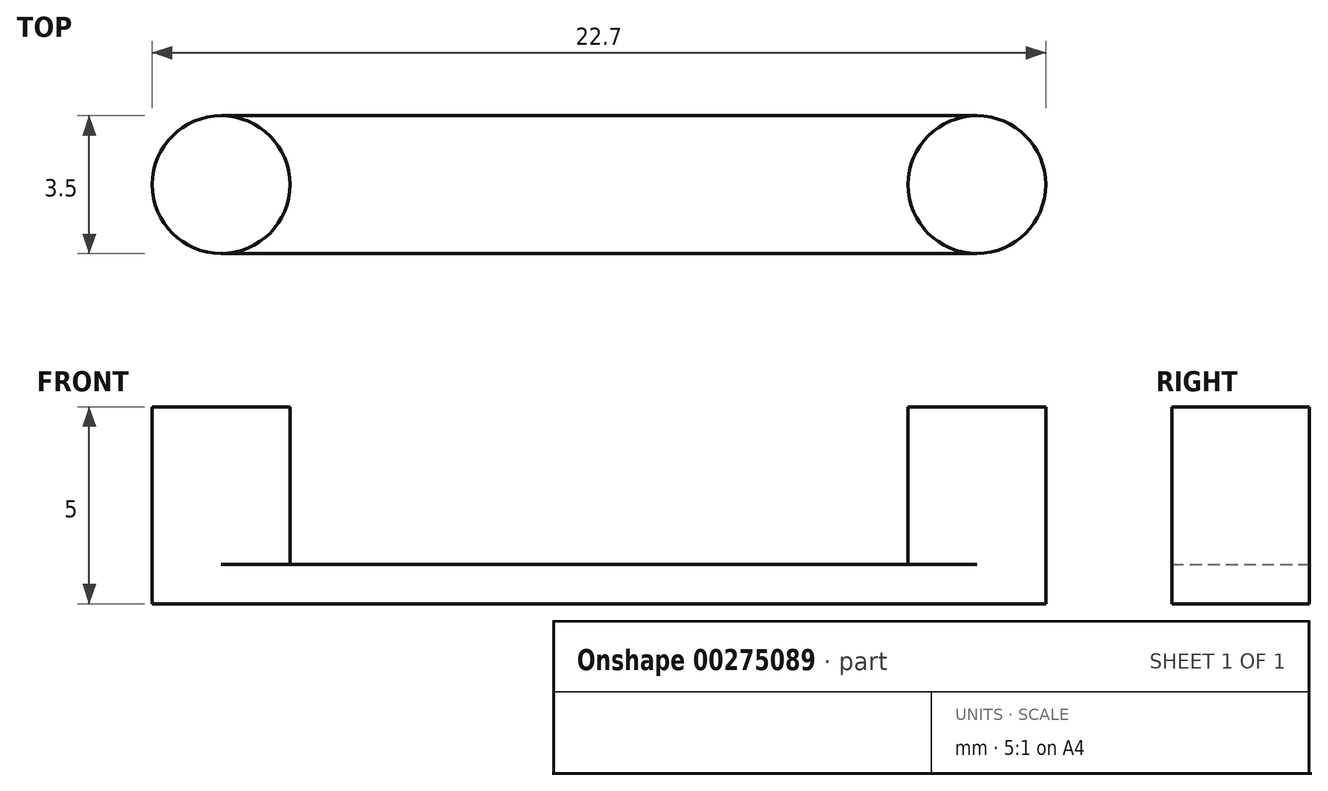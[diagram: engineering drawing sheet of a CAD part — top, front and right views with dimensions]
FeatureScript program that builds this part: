
annotation { "Feature Type Name" : "Feature", "Feature Type Description" : "" }
export const myFeature = defineFeature(function(context is Context, id is Id, definition is map)
    precondition{}
    {
        {
            var Q0;
            Q0=qCreatedBy(makeId("Top.planeOp"),FACE);
            var sketch = newSketch(context, id + "F0", { "sketchPlane" : qUnion([Q0])});
            skLineSegment(sketch, "E0.bottom", {"start": v(9.6, -9.6) * mm, "end": v(-9.6, -9.6) * mm, "construction": true});
            skLineSegment(sketch, "E0.top", {"start": v(9.6, 9.6) * mm, "end": v(-9.6, 9.6) * mm, "construction": true});
            skLineSegment(sketch, "E0.left", {"start": v(9.6, -9.6) * mm, "end": v(9.6, 9.6) * mm, "construction": true});
            skLineSegment(sketch, "E0.right", {"start": v(-9.6, -9.6) * mm, "end": v(-9.6, 9.6) * mm, "construction": true});
            skPoint(sketch, "E0.middle", {"position": v(0, 0) * mm});
            skPoint(sketch, "E1", {"position": v(-9.6, 0) * mm});
            skPoint(sketch, "E2", {"position": v(9.6, 0) * mm});
            skLineSegment(sketch, "E3", {"start": v(9.6, 0) * mm, "end": v(-9.6, 0) * mm});
            skCircle(sketch, "E4", {"center": v(-9.6, 0) * mm, "radius": 1.75 * mm});
            skCircle(sketch, "E5", {"center": v(9.6, 0) * mm, "radius": 1.75 * mm});
            skLineSegment(sketch, "E6.bottom", {"start": v(-9.6, -1.75) * mm, "end": v(9.6, -1.75) * mm});
            skLineSegment(sketch, "E6.top", {"start": v(-9.6, 1.75) * mm, "end": v(9.6, 1.75) * mm});
            skLineSegment(sketch, "E6.left", {"start": v(-9.6, -1.75) * mm, "end": v(-9.6, 1.75) * mm});
            skLineSegment(sketch, "E6.right", {"start": v(9.6, -1.75) * mm, "end": v(9.6, 1.75) * mm});
            skSolve(sketch);
        }
        {
            var Q0;
            {var subQ5=sQuery(id+"F0.wireOp",EDGE,"E6.top");Q0=makeQuery(id+"F0.imprint","IMPRINT",FACE,{"disambiguationData":[TD([[makeQuery(id+"F0.imprint","IMPRINT",EDGE,{"derivedFrom":subQ5}),-1.0]])]});}
            var Q1;
            {var subQ5=sQuery(id+"F0.wireOp",EDGE,"E6.bottom");Q1=makeQuery(id+"F0.imprint","IMPRINT",FACE,{"disambiguationData":[TD([[makeQuery(id+"F0.imprint","IMPRINT",EDGE,{"derivedFrom":subQ5}),1.0]])]});}
            extrude(context, id + "F1", {"entities" : qUnion([Q0, Q1]), "depth" : 1 * mm});
        }
        {
            var Q0;
            {var subQ0=sQuery(id+"F0.wireOp",EDGE,"E6.right");var subQ4=makeQuery(id+"F0.imprint","INTERSECT",VERTEX,{"derivedFrom":[sQuery(id+"F0.wireOp",EDGE,"E3"),subQ0]});Q0=makeQuery(id+"F0.imprint","IMPRINT",FACE,{"disambiguationData":[TD([[makeQuery(id+"F0.imprint","IMPRINT",EDGE,{"disambiguationData":[TD([[subQ4,1.0]])],"derivedFrom":subQ0}),-1.0]])]});}
            var Q1;
            {var subQ0=sQuery(id+"F0.wireOp",EDGE,"E6.right");var subQ1=sQuery(id+"F0.wireOp",EDGE,"E3");var subQ2=makeQuery(id+"F0.imprint","INTERSECT",VERTEX,{"derivedFrom":[subQ1,subQ0]});Q1=makeQuery(id+"F0.imprint","IMPRINT",FACE,{"disambiguationData":[TD([[makeQuery(id+"F0.imprint","IMPRINT",EDGE,{"disambiguationData":[TD([[subQ2,-1.0]])],"derivedFrom":subQ1}),-1.0]])]});}
            var Q2;
            {var subQ0=sQuery(id+"F0.wireOp",EDGE,"E6.right");var subQ1=sQuery(id+"F0.wireOp",EDGE,"E3");var subQ2=makeQuery(id+"F0.imprint","INTERSECT",VERTEX,{"derivedFrom":[subQ1,subQ0]});Q2=makeQuery(id+"F0.imprint","IMPRINT",FACE,{"disambiguationData":[TD([[makeQuery(id+"F0.imprint","IMPRINT",EDGE,{"disambiguationData":[TD([[subQ2,-1.0]])],"derivedFrom":subQ1}),1.0]])]});}
            var Q3;
            {var subQ0=sQuery(id+"F0.wireOp",EDGE,"E6.left");var subQ1=sQuery(id+"F0.wireOp",EDGE,"E3");var subQ2=makeQuery(id+"F0.imprint","INTERSECT",VERTEX,{"derivedFrom":[subQ1,subQ0]});Q3=makeQuery(id+"F0.imprint","IMPRINT",FACE,{"disambiguationData":[TD([[makeQuery(id+"F0.imprint","IMPRINT",EDGE,{"disambiguationData":[TD([[subQ2,1.0]])],"derivedFrom":subQ1}),-1.0]])]});}
            var Q4;
            {var subQ0=sQuery(id+"F0.wireOp",EDGE,"E6.left");var subQ1=sQuery(id+"F0.wireOp",EDGE,"E3");var subQ2=makeQuery(id+"F0.imprint","INTERSECT",VERTEX,{"derivedFrom":[subQ1,subQ0]});Q4=makeQuery(id+"F0.imprint","IMPRINT",FACE,{"disambiguationData":[TD([[makeQuery(id+"F0.imprint","IMPRINT",EDGE,{"disambiguationData":[TD([[subQ2,1.0]])],"derivedFrom":subQ1}),1.0]])]});}
            var Q5;
            {var subQ0=sQuery(id+"F0.wireOp",EDGE,"E6.left");var subQ4=makeQuery(id+"F0.imprint","INTERSECT",VERTEX,{"derivedFrom":[sQuery(id+"F0.wireOp",EDGE,"E3"),subQ0]});Q5=makeQuery(id+"F0.imprint","IMPRINT",FACE,{"disambiguationData":[TD([[makeQuery(id+"F0.imprint","IMPRINT",EDGE,{"disambiguationData":[TD([[subQ4,1.0]])],"derivedFrom":subQ0}),1.0]])]});}
            extrude(context, id + "F2", {"entities" : qUnion([Q0, Q1, Q2, Q3, Q4, Q5]), "operationType" : NewBodyOperationType.ADD, "depth" : 5 * mm});
        }
    });
